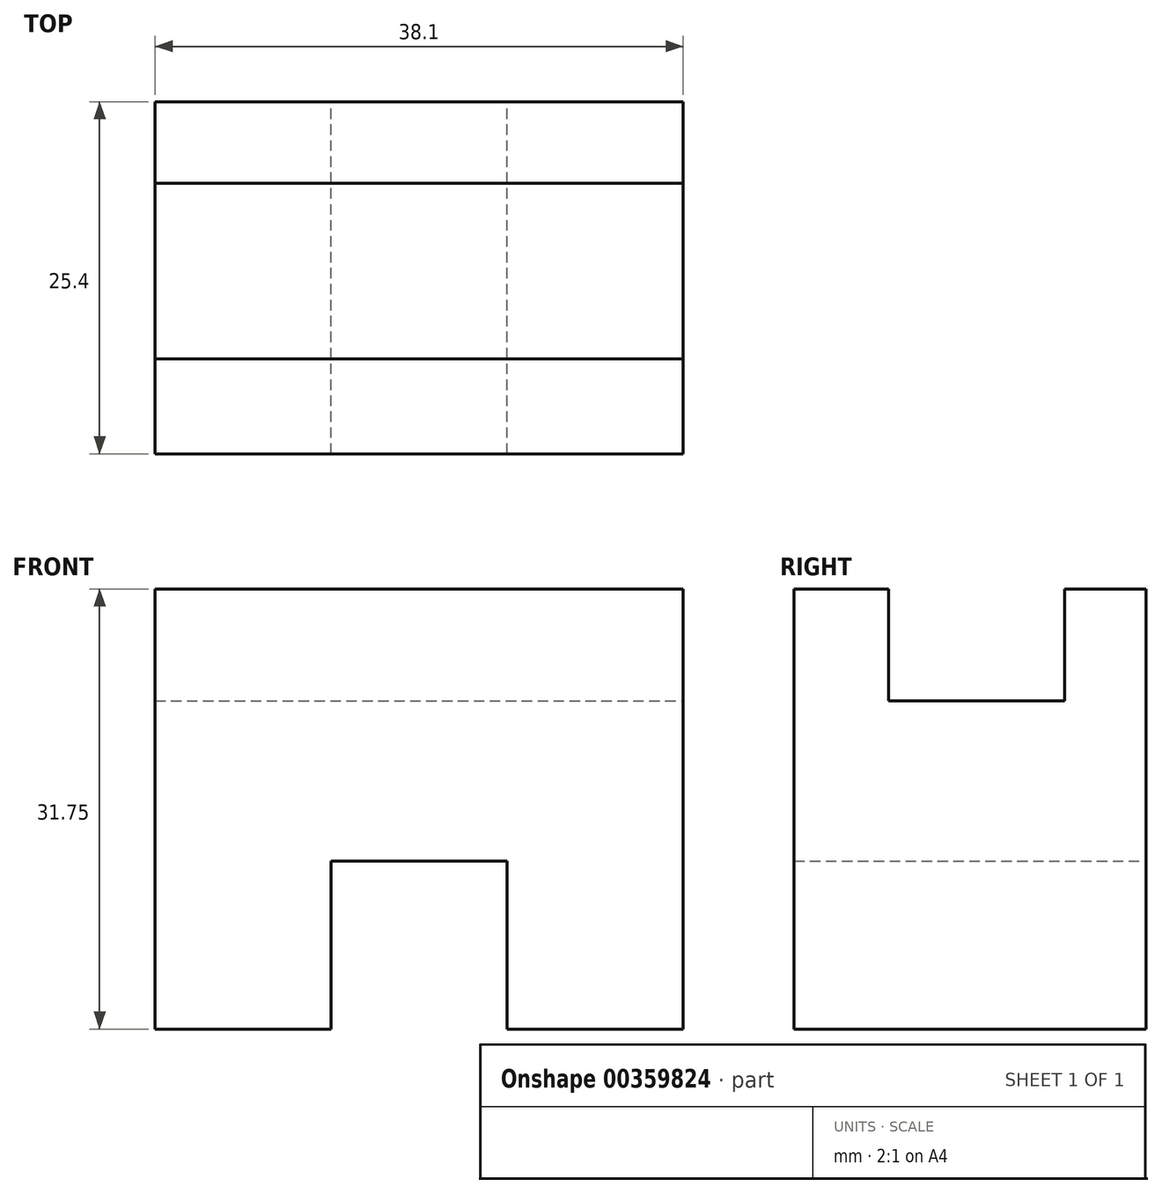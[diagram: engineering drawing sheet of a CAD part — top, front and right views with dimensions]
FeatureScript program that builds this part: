
annotation { "Feature Type Name" : "Feature", "Feature Type Description" : "" }
export const myFeature = defineFeature(function(context is Context, id is Id, definition is map)
    precondition{}
    {
        {
            var Q0;
            Q0=qCreatedBy(makeId("Front.planeOp"),FACE);
            var sketch = newSketch(context, id + "F0", { "sketchPlane" : qUnion([Q0])});
            skLineSegment(sketch, "E0", {"start": v(0, 0) * mm, "end": v(12.7, 0) * mm});
            skLineSegment(sketch, "E1", {"start": v(12.7, 0) * mm, "end": v(12.7, 12.13) * mm});
            skLineSegment(sketch, "E2", {"start": v(12.7, 12.13) * mm, "end": v(25.4, 12.13) * mm});
            skLineSegment(sketch, "E3", {"start": v(25.4, 12.13) * mm, "end": v(25.4, 0) * mm});
            skLineSegment(sketch, "E4", {"start": v(25.4, 0) * mm, "end": v(38.1, 0) * mm});
            skLineSegment(sketch, "E5", {"start": v(38.1, 0) * mm, "end": v(38.1, 31.75) * mm});
            skLineSegment(sketch, "E6", {"start": v(38.1, 31.75) * mm, "end": v(0, 31.75) * mm});
            skLineSegment(sketch, "E7", {"start": v(0, 31.75) * mm, "end": v(0, 0) * mm});
            skSolve(sketch);
        }
        {
            var Q0;
            Q0 = qSketchRegion(id + "F0", true);
            var Q1;
            Q1=makeQuery(id+"F0.imprint","IMPRINT",FACE,{"disambiguationData":[TD([[makeQuery(id+"F0.imprint","IMPRINT",EDGE,{"derivedFrom":sQuery(id+"F0.wireOp",EDGE,"E0")}),1.0]])]});
            extrude(context, id + "F1", {"entities" : qUnion([Q0, Q1]), "depth" : 25.4 * mm});
        }
        {
            var Q0;
            Q0=makeQuery(id+"F1.opExtrude","SWEPT_FACE",FACE,{"disambiguationData":[OSD([sQuery(id+"F0.wireOp",EDGE,"E5")])]});
            var sketch = newSketch(context, id + "F2", { "sketchPlane" : qUnion([Q0])});
            skLineSegment(sketch, "E8", {"start": v(-18.57, 31.75) * mm, "end": v(-18.57, 23.68) * mm});
            skLineSegment(sketch, "E9", {"start": v(-18.57, 23.68) * mm, "end": v(-5.88, 23.68) * mm});
            skLineSegment(sketch, "E10", {"start": v(-5.88, 23.68) * mm, "end": v(-5.88, 31.75) * mm});
            skSolve(sketch);
        }
        {
            var Q0;
            {var subQ0=sQuery(id+"F2.wireOp",EDGE,"E8");Q0=makeQuery(id+"F2.imprint","IMPRINT",FACE,{"disambiguationData":[TD([[makeQuery(id+"F2.imprint","IMPRINT",EDGE,{"derivedFrom":subQ0}),1.0]])]});}
            extrude(context, id + "F3", {"entities" : qUnion([Q0]), "operationType" : NewBodyOperationType.REMOVE, "oppositeDirection" : true, "depth" : 38.1 * mm});
        }
    });
